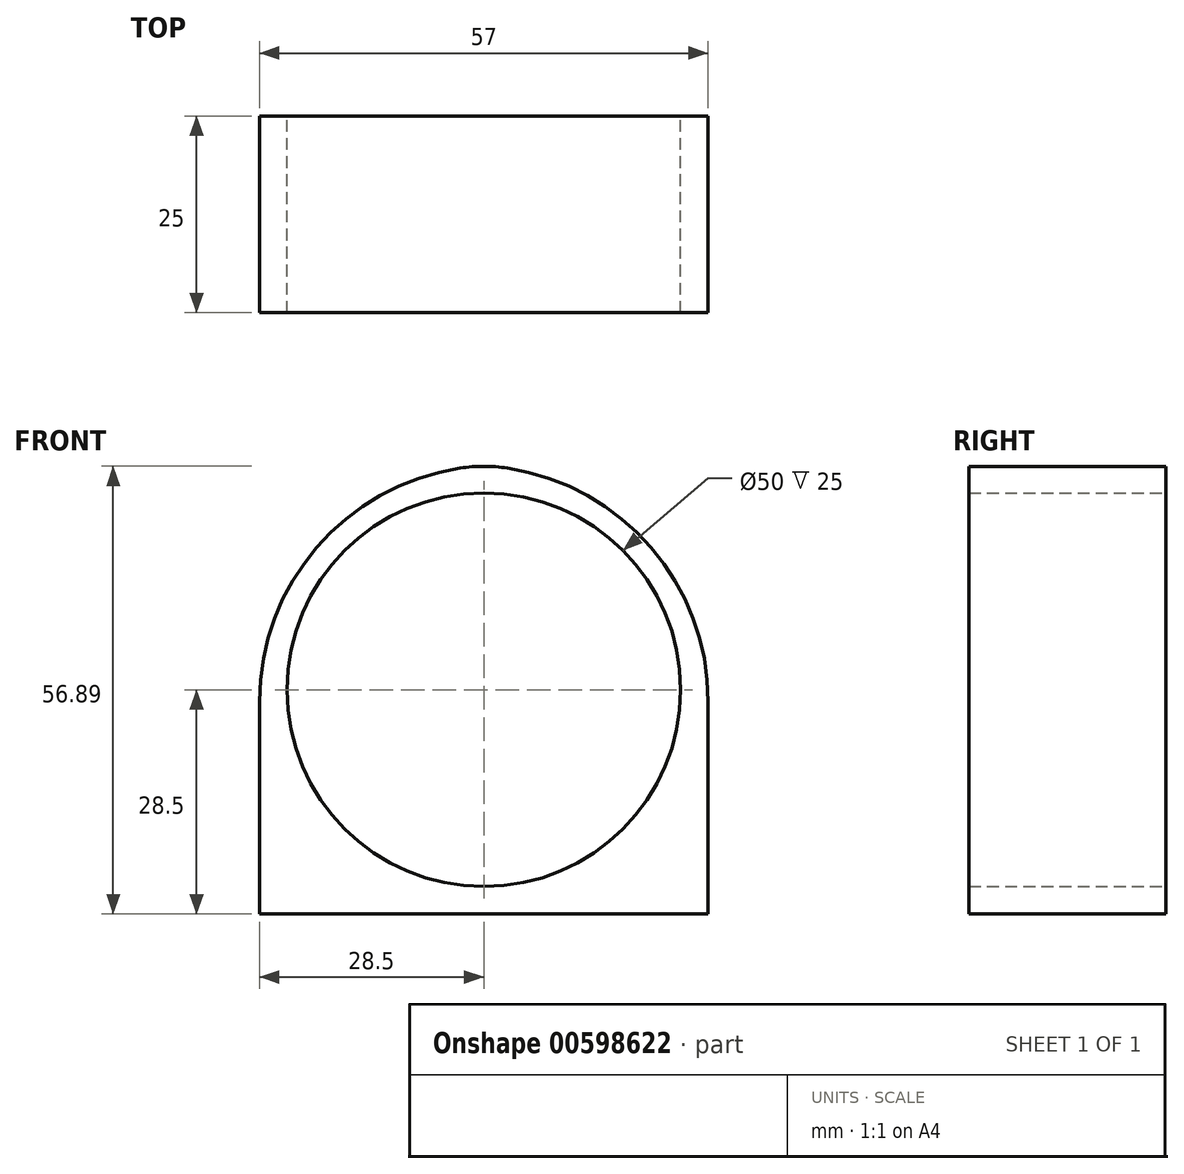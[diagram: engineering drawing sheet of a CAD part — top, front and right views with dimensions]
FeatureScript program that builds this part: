
annotation { "Feature Type Name" : "Feature", "Feature Type Description" : "" }
export const myFeature = defineFeature(function(context is Context, id is Id, definition is map)
    precondition{}
    {
        {
            var Q0;
            Q0=qCreatedBy(makeId("Front.planeOp"),FACE);
            var sketch = newSketch(context, id + "F0", { "sketchPlane" : qUnion([Q0])});
            skCircle(sketch, "E0", {"center": v(0, 0) * mm, "radius": 25 * mm});
            skLineSegment(sketch, "E1.bottom", {"start": v(28.5, -28.5) * mm, "end": v(-28.5, -28.5) * mm});
            skLineSegment(sketch, "E1.top", {"start": v(28.5, 28.5) * mm, "end": v(-28.5, 28.5) * mm});
            skLineSegment(sketch, "E1.left", {"start": v(28.5, -28.5) * mm, "end": v(28.5, 28.5) * mm});
            skLineSegment(sketch, "E1.right", {"start": v(-28.5, -28.5) * mm, "end": v(-28.5, 28.5) * mm});
            skSolve(sketch);
        }
        {
            var Q0;
            Q0=makeQuery(id+"F0.imprint","IMPRINT",FACE,{"disambiguationData":[TD([[makeQuery(id+"F0.imprint","IMPRINT",EDGE,{"derivedFrom":sQuery(id+"F0.wireOp",EDGE,"E0")}),-1.0]])]});
            extrude(context, id + "F1", {"entities" : qUnion([Q0]), "depth" : 25 * mm, "offsetDistance" : 25 * mm});
        }
        {
            var Q0;
            Q0=makeQuery(id+"F1.opExtrude","SWEPT_EDGE",EDGE,{"disambiguationData":[OSD([sQuery(id+"F0.wireOp",EDGE,"E1.top"),sQuery(id+"F0.wireOp",EDGE,"E1.left")])]});
            var Q1;
            Q1=makeQuery(id+"F1.opExtrude","SWEPT_EDGE",EDGE,{"disambiguationData":[OSD([sQuery(id+"F0.wireOp",EDGE,"E1.top"),sQuery(id+"F0.wireOp",EDGE,"E1.right")])]});
            fillet(context, id + "F2", {"entities" : qUnion([Q0, Q1]), "radius" : 30 * mm, "tangentPropagation" : true, "allowEdgeOverflow" : false});
        }
        {
            var Q0;
            {var subQ0=sQuery(id+"F0.wireOp",EDGE,"E1.top");Q0=makeQuery(id+"F2.opFillet","BLEND_EDGE",EDGE,{"blendedFrom":[makeQuery(id+"F1.opExtrude","SWEPT_EDGE",EDGE,{"disambiguationData":[OSD([subQ0,sQuery(id+"F0.wireOp",EDGE,"E1.left")])]}),makeQuery(id+"F1.opExtrude","SWEPT_EDGE",EDGE,{"disambiguationData":[OSD([subQ0,sQuery(id+"F0.wireOp",EDGE,"E1.right")])]})],"blendedInto":[]});}
            fillet(context, id + "F3", {"entities" : qUnion([Q0]), "radius" : 20 * mm, "tangentPropagation" : true, "allowEdgeOverflow" : false});
        }
    });
